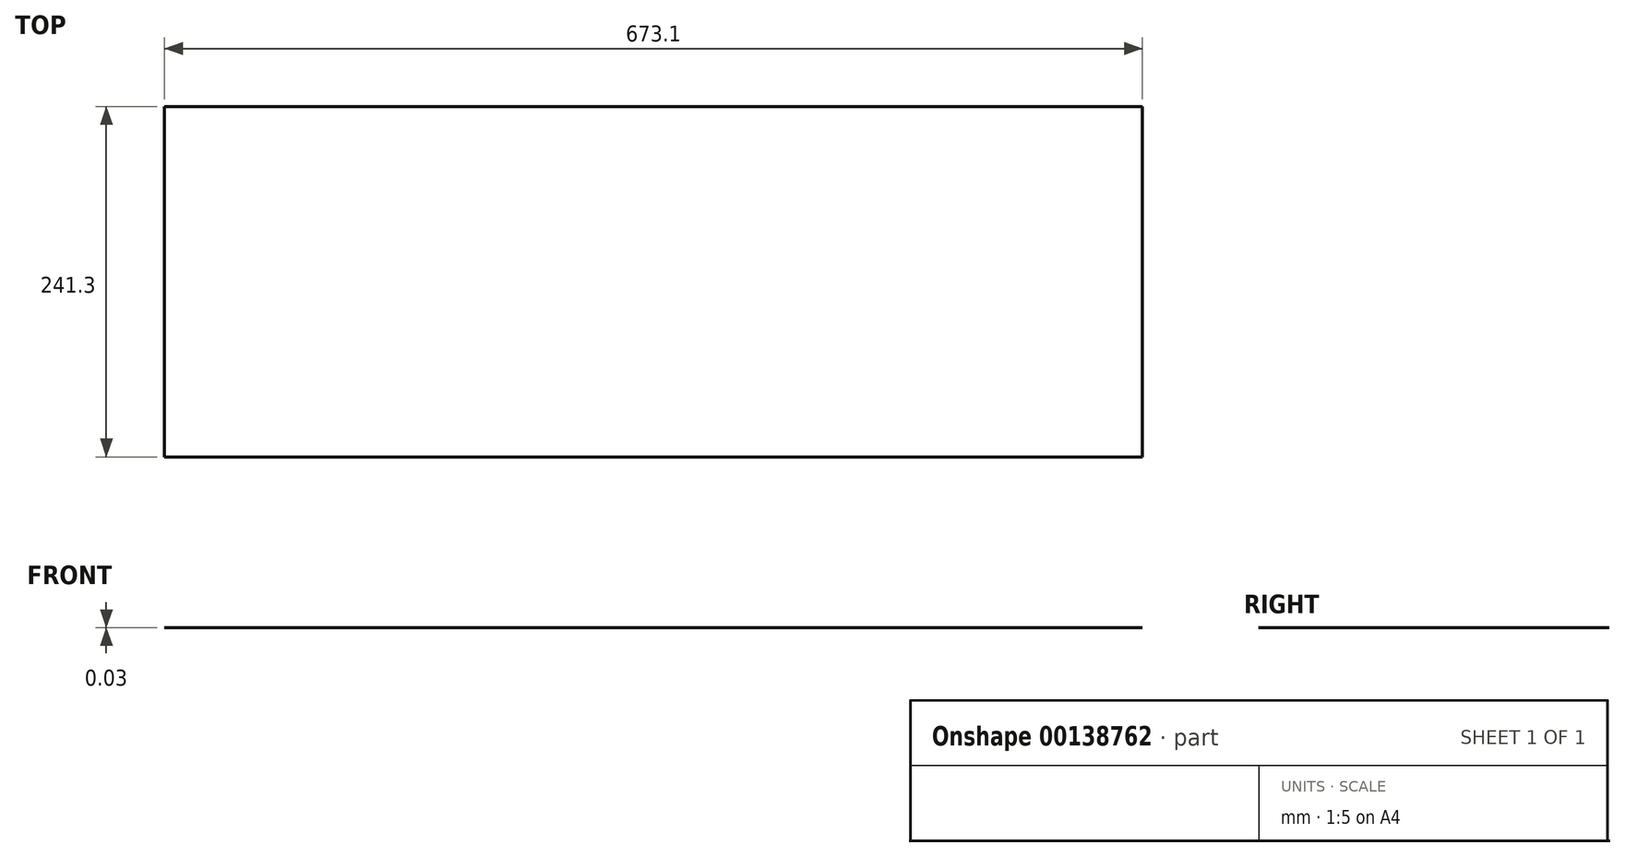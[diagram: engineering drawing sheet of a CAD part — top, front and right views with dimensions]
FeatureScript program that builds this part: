
annotation { "Feature Type Name" : "Feature", "Feature Type Description" : "" }
export const myFeature = defineFeature(function(context is Context, id is Id, definition is map)
    precondition{}
    {
        {
            var Q0;
            Q0=qCreatedBy(makeId("Top.planeOp"),FACE);
            var sketch = newSketch(context, id + "F0", { "sketchPlane" : qUnion([Q0])});
            skLineSegment(sketch, "E0.bottom", {"start": v(-336.55, 120.65) * mm, "end": v(336.55, 120.65) * mm});
            skLineSegment(sketch, "E0.top", {"start": v(-336.55, -120.65) * mm, "end": v(336.55, -120.65) * mm});
            skLineSegment(sketch, "E0.left", {"start": v(-336.55, 120.65) * mm, "end": v(-336.55, -120.65) * mm});
            skLineSegment(sketch, "E0.right", {"start": v(336.55, 120.65) * mm, "end": v(336.55, -120.65) * mm});
            skPoint(sketch, "E0.middle", {"position": v(0, 0) * mm});
            skSolve(sketch);
        }
        {
            var Q0;
            Q0=makeQuery(id+"F0.imprint","IMPRINT",FACE,{"disambiguationData":[TD([[makeQuery(id+"F0.imprint","IMPRINT",EDGE,{"derivedFrom":sQuery(id+"F0.wireOp",EDGE,"E0.bottom")}),-1.0]])]});
            extrude(context, id + "F1", {"entities" : qUnion([Q0]), "depth" : 3 / 101.6 * mm});
        }
    });
